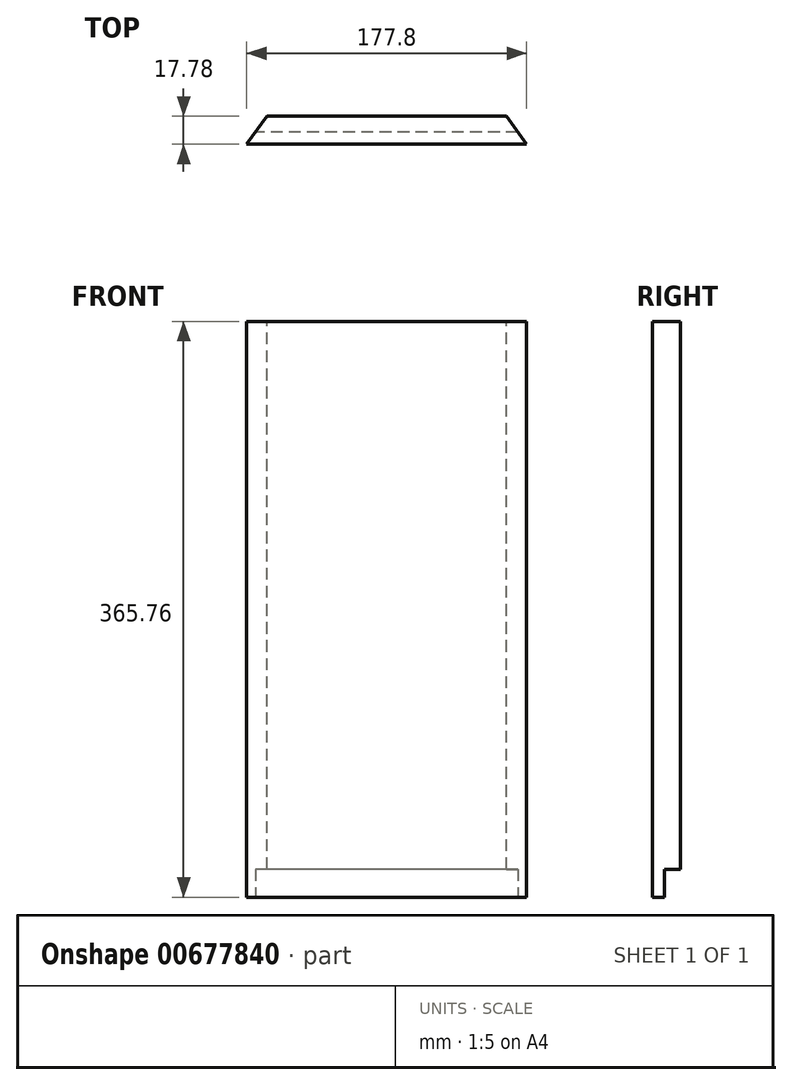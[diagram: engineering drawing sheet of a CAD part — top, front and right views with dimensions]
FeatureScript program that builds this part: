
annotation { "Feature Type Name" : "Feature", "Feature Type Description" : "" }
export const myFeature = defineFeature(function(context is Context, id is Id, definition is map)
    precondition{}
    {
        {
            var Q0;
            Q0=qCreatedBy(makeId("Front.planeOp"),FACE);
            var sketch = newSketch(context, id + "F0", { "sketchPlane" : qUnion([Q0])});
            skLineSegment(sketch, "E0.bottom", {"start": v(88.9, 0) * mm, "end": v(-88.9, 0) * mm});
            skLineSegment(sketch, "E0.top", {"start": v(88.9, 365.76) * mm, "end": v(-88.9, 365.76) * mm});
            skLineSegment(sketch, "E0.left", {"start": v(88.9, 0) * mm, "end": v(88.9, 365.76) * mm});
            skLineSegment(sketch, "E0.right", {"start": v(-88.9, 0) * mm, "end": v(-88.9, 365.76) * mm});
            skSolve(sketch);
        }
        {
            var Q0;
            Q0=makeQuery(id+"F0.imprint","IMPRINT",FACE,{"disambiguationData":[TD([[makeQuery(id+"F0.imprint","IMPRINT",EDGE,{"derivedFrom":sQuery(id+"F0.wireOp",EDGE,"E0.bottom")}),-1.0]])]});
            extrude(context, id + "F1", {"entities" : qUnion([Q0]), "depth" : 17.78 * mm, "offsetDistance" : 25.4 * mm});
        }
        {
            var Q0;
            Q0=makeQuery(id+"F1.opExtrude","CAP_FACE",FACE,{"disambiguationData":[OSD([sQuery(id+"F0.wireOp",EDGE,"E0.bottom"),sQuery(id+"F0.wireOp",EDGE,"E0.top"),sQuery(id+"F0.wireOp",EDGE,"E0.left"),sQuery(id+"F0.wireOp",EDGE,"E0.right")])],"isStart":true});
            var sketch = newSketch(context, id + "F2", { "sketchPlane" : qUnion([Q0])});
            skLineSegment(sketch, "E1.bottom", {"start": v(-88.9, 0) * mm, "end": v(88.9, 0) * mm});
            skLineSegment(sketch, "E1.top", {"start": v(-88.9, 17.78) * mm, "end": v(88.9, 17.78) * mm});
            skLineSegment(sketch, "E1.left", {"start": v(-88.9, 0) * mm, "end": v(-88.9, 17.78) * mm});
            skLineSegment(sketch, "E1.right", {"start": v(88.9, 0) * mm, "end": v(88.9, 17.78) * mm});
            skSolve(sketch);
        }
        {
            var Q0;
            Q0 = qSketchRegion(id + "F2", true);
            extrude(context, id + "F3", {"entities" : qUnion([Q0]), "operationType" : NewBodyOperationType.REMOVE, "oppositeDirection" : true, "depth" : 10.16 * mm, "offsetDistance" : 25.4 * mm});
        }
        {
            var Q0;
            Q0=makeQuery(id+"F1.opExtrude","SWEPT_FACE",FACE,{"disambiguationData":[OSD([sQuery(id+"F0.wireOp",EDGE,"E0.top")])]});
            var sketch = newSketch(context, id + "F4", { "sketchPlane" : qUnion([Q0])});
            skLineSegment(sketch, "E2", {"start": v(-88.9, -17.78) * mm, "end": v(-75.98, 0) * mm});
            skLineSegment(sketch, "E3", {"start": v(-75.98, 0) * mm, "end": v(-88.9, 0) * mm});
            skLineSegment(sketch, "E4", {"start": v(-88.9, 0) * mm, "end": v(-88.9, -17.78) * mm});
            skLineSegment(sketch, "E5", {"start": v(88.9, -17.78) * mm, "end": v(75.98, 0) * mm});
            skLineSegment(sketch, "E6", {"start": v(75.98, 0) * mm, "end": v(88.9, 0) * mm});
            skLineSegment(sketch, "E7", {"start": v(88.9, 0) * mm, "end": v(88.9, -17.78) * mm});
            skSolve(sketch);
        }
        {
            var Q0;
            Q0 = qSketchRegion(id + "F4", true);
            extrude(context, id + "F5", {"entities" : qUnion([Q0]), "operationType" : NewBodyOperationType.REMOVE, "endBound" : BoundingType.THROUGH_ALL, "oppositeDirection" : true, "depth" : 25.4 * mm, "offsetDistance" : 25.4 * mm});
        }
    });
